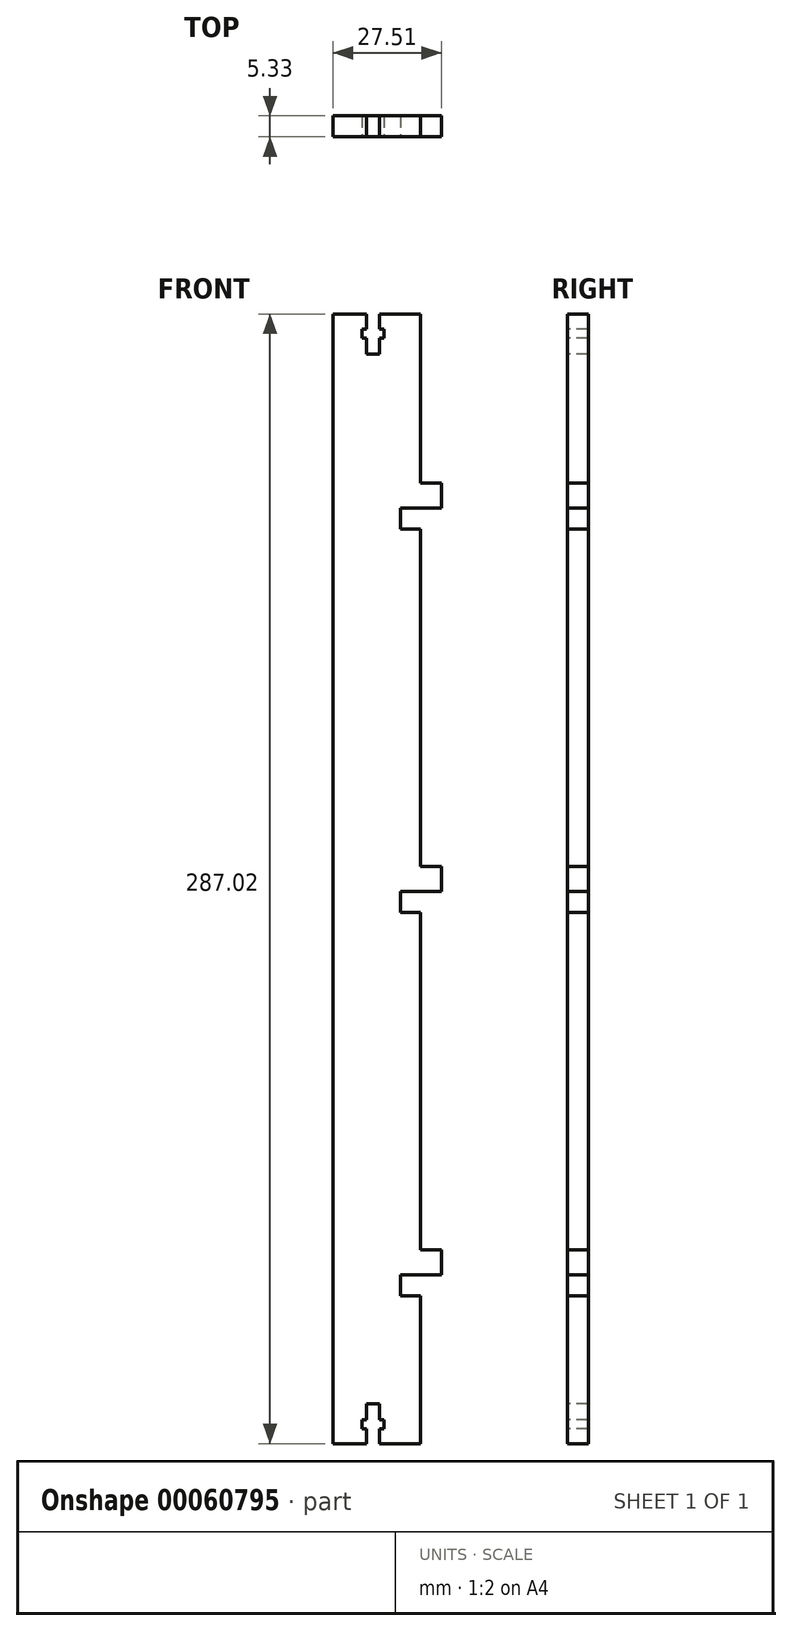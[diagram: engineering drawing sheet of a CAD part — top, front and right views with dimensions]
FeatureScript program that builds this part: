
annotation { "Feature Type Name" : "Feature", "Feature Type Description" : "" }
export const myFeature = defineFeature(function(context is Context, id is Id, definition is map)
    precondition{}
    {
        {
            var Q0;
            Q0=qCreatedBy(makeId("Front.planeOp"),FACE);
            var sketch = newSketch(context, id + "F0", { "sketchPlane" : qUnion([Q0])});
            skLineSegment(sketch, "E0.bottom", {"start": v(-34.55, 214.35) * mm, "end": v(-12.38, 214.35) * mm});
            skLineSegment(sketch, "E0.top", {"start": v(-34.55, -77.75) * mm, "end": v(-12.38, -77.75) * mm});
            skLineSegment(sketch, "E0.left", {"start": v(-34.55, 214.35) * mm, "end": v(-34.55, -77.75) * mm});
            skLineSegment(sketch, "E0.right", {"start": v(-12.38, 214.35) * mm, "end": v(-12.38, -77.75) * mm});
            skSolve(sketch);
        }
        {
            var Q0;
            Q0=makeQuery(id+"F0.imprint","IMPRINT",FACE,{"disambiguationData":[TD([[makeQuery(id+"F0.imprint","IMPRINT",EDGE,{"derivedFrom":sQuery(id+"F0.wireOp",EDGE,"E0.bottom")}),-1.0]])]});
            extrude(context, id + "F1", {"entities" : qUnion([Q0]), "depth" : 5.33 * mm});
        }
        {
            var Q0;
            Q0=makeQuery(id+"F1.opExtrude","SWEPT_FACE",FACE,{"disambiguationData":[OSD([sQuery(id+"F0.wireOp",EDGE,"E0.right")])]});
            var sketch = newSketch(context, id + "F2", { "sketchPlane" : qUnion([Q0])});
            skLineSegment(sketch, "E1.bottom", {"start": v(-5.33, 168.88) * mm, "end": v(0, 168.88) * mm});
            skLineSegment(sketch, "E1.top", {"start": v(-5.33, 162.53) * mm, "end": v(0, 162.53) * mm});
            skLineSegment(sketch, "E1.left", {"start": v(-5.33, 168.88) * mm, "end": v(-5.33, 162.53) * mm});
            skLineSegment(sketch, "E1.right", {"start": v(0, 168.88) * mm, "end": v(0, 162.53) * mm});
            skLineSegment(sketch, "E2.bottom", {"start": v(-5.33, 71.47) * mm, "end": v(0, 71.47) * mm});
            skLineSegment(sketch, "E2.top", {"start": v(-5.33, 65.12) * mm, "end": v(0, 65.12) * mm});
            skLineSegment(sketch, "E2.left", {"start": v(-5.33, 71.47) * mm, "end": v(-5.33, 65.12) * mm});
            skLineSegment(sketch, "E2.right", {"start": v(0, 71.47) * mm, "end": v(0, 65.12) * mm});
            skLineSegment(sketch, "E3.bottom", {"start": v(0, -25.94) * mm, "end": v(-5.33, -25.94) * mm});
            skLineSegment(sketch, "E3.top", {"start": v(0, -32.29) * mm, "end": v(-5.33, -32.29) * mm});
            skLineSegment(sketch, "E3.left", {"start": v(0, -25.94) * mm, "end": v(0, -32.29) * mm});
            skLineSegment(sketch, "E3.right", {"start": v(-5.33, -25.94) * mm, "end": v(-5.33, -32.29) * mm});
            skSolve(sketch);
        }
        {
            var Q0;
            Q0=makeQuery(id+"F2.imprint","IMPRINT",FACE,{"disambiguationData":[TD([[makeQuery(id+"F2.imprint","IMPRINT",EDGE,{"derivedFrom":sQuery(id+"F2.wireOp",EDGE,"E1.bottom")}),-1.0]])]});
            var Q1;
            Q1=makeQuery(id+"F2.imprint","IMPRINT",FACE,{"disambiguationData":[TD([[makeQuery(id+"F2.imprint","IMPRINT",EDGE,{"derivedFrom":sQuery(id+"F2.wireOp",EDGE,"E2.bottom")}),-1.0]])]});
            var Q2;
            Q2=makeQuery(id+"F2.imprint","IMPRINT",FACE,{"disambiguationData":[TD([[makeQuery(id+"F2.imprint","IMPRINT",EDGE,{"derivedFrom":sQuery(id+"F2.wireOp",EDGE,"E3.bottom")}),1.0]])]});
            extrude(context, id + "F3", {"entities" : qUnion([Q0, Q1, Q2]), "operationType" : NewBodyOperationType.ADD, "depth" : 5.33 * mm});
        }
        {
            var Q0;
            Q0=makeQuery(id+"F1.opExtrude","CAP_FACE",FACE,{"disambiguationData":[OSD([sQuery(id+"F0.wireOp",EDGE,"E0.bottom"),sQuery(id+"F0.wireOp",EDGE,"E0.top"),sQuery(id+"F0.wireOp",EDGE,"E0.left"),sQuery(id+"F0.wireOp",EDGE,"E0.right")])],"isStart":false});
            var sketch = newSketch(context, id + "F4", { "sketchPlane" : qUnion([Q0])});
            skLineSegment(sketch, "E4", {"start": v(-22.28, 68.3) * mm, "end": v(-43.85, 68.3) * mm});
            skLineSegment(sketch, "E5.left", {"start": v(-26.04, -77.75) * mm, "end": v(-26.04, -71.4) * mm});
            skLineSegment(sketch, "E5.right", {"start": v(-22.74, -77.75) * mm, "end": v(-22.74, -71.4) * mm});
            skLineSegment(sketch, "E6.0", {"start": v(-26.04, -71.4) * mm, "end": v(-27.19, -71.4) * mm});
            skLineSegment(sketch, "E7.bottom", {"start": v(-27.19, -71.4) * mm, "end": v(-26.04, -71.4) * mm});
            skLineSegment(sketch, "E7.top", {"start": v(-27.19, -69.12) * mm, "end": v(-26.04, -69.12) * mm});
            skLineSegment(sketch, "E7.left", {"start": v(-27.19, -71.4) * mm, "end": v(-27.19, -69.12) * mm});
            skLineSegment(sketch, "E7.right", {"start": v(-21.6, -71.4) * mm, "end": v(-21.6, -69.12) * mm});
            skLineSegment(sketch, "E8.trimOffspring", {"start": v(-26.04, -69.12) * mm, "end": v(-26.04, -65.05) * mm});
            skLineSegment(sketch, "E9.trimOffspring", {"start": v(-22.74, -69.12) * mm, "end": v(-22.74, -65.05) * mm});
            skLineSegment(sketch, "E10.trimOffspring", {"start": v(-22.74, -71.4) * mm, "end": v(-21.6, -71.4) * mm});
            skLineSegment(sketch, "E11.trimOffspring", {"start": v(-22.74, -69.12) * mm, "end": v(-21.6, -69.12) * mm});
            skLineSegment(sketch, "E12", {"start": v(-26.04, -77.75) * mm, "end": v(-22.74, -77.75) * mm});
            skLineSegment(sketch, "E13.0", {"start": v(-26.04, -65.05) * mm, "end": v(-22.74, -65.05) * mm});
            skLineSegment(sketch, "E14.MirrorCS", {"start": v(-26.04, 208) * mm, "end": v(-27.19, 208) * mm});
            skLineSegment(sketch, "E15.MirrorCS", {"start": v(-27.19, 208) * mm, "end": v(-26.04, 208) * mm});
            skLineSegment(sketch, "E16.MirrorCS", {"start": v(-21.6, 208) * mm, "end": v(-21.6, 205.7) * mm});
            skLineSegment(sketch, "E17.MirrorCS", {"start": v(-22.74, 208) * mm, "end": v(-21.6, 208) * mm});
            skLineSegment(sketch, "E18.MirrorCS", {"start": v(-22.74, 205.7) * mm, "end": v(-21.6, 205.7) * mm});
            skLineSegment(sketch, "E19.MirrorCS", {"start": v(-26.04, 214.35) * mm, "end": v(-22.74, 214.35) * mm});
            skLineSegment(sketch, "E20.MirrorCS", {"start": v(-27.19, 205.7) * mm, "end": v(-26.04, 205.7) * mm});
            skLineSegment(sketch, "E21.MirrorCS", {"start": v(-27.19, 208) * mm, "end": v(-27.19, 205.7) * mm});
            skLineSegment(sketch, "E22.MirrorCS", {"start": v(-26.04, 201.65) * mm, "end": v(-22.74, 201.65) * mm});
            skLineSegment(sketch, "E23.MirrorCS", {"start": v(-22.74, 214.35) * mm, "end": v(-22.74, 208) * mm});
            skLineSegment(sketch, "E24.MirrorCS", {"start": v(-22.74, 205.7) * mm, "end": v(-22.74, 201.65) * mm});
            skLineSegment(sketch, "E25.MirrorCS", {"start": v(-26.04, 214.35) * mm, "end": v(-26.04, 208) * mm});
            skLineSegment(sketch, "E26.MirrorCS", {"start": v(-26.04, 205.7) * mm, "end": v(-26.04, 201.65) * mm});
            skSolve(sketch);
        }
        {
            var Q0;
            Q0 = qSketchRegion(id + "F4", true);
            extrude(context, id + "F5", {"entities" : qUnion([Q0]), "operationType" : NewBodyOperationType.REMOVE, "endBound" : BoundingType.THROUGH_ALL, "oppositeDirection" : true, "depth" : 25.4 * mm});
        }
        {
            var Q0;
            Q0=makeQuery(id+"F3.boolean.opBoolean","MERGE",FACE,{"derivedFrom":[makeQuery(id+"F1.opExtrude","CAP_FACE",FACE,{"disambiguationData":[OSD([sQuery(id+"F0.wireOp",EDGE,"E0.bottom"),sQuery(id+"F0.wireOp",EDGE,"E0.top"),sQuery(id+"F0.wireOp",EDGE,"E0.left"),sQuery(id+"F0.wireOp",EDGE,"E0.right")])],"isStart":false}),makeQuery(id+"F3.opExtrude","SWEPT_FACE",FACE,{"disambiguationData":[OSD([sQuery(id+"F2.wireOp",EDGE,"E1.left")])]}),makeQuery(id+"F3.opExtrude","SWEPT_FACE",FACE,{"disambiguationData":[OSD([sQuery(id+"F2.wireOp",EDGE,"E2.left")])]}),makeQuery(id+"F3.opExtrude","SWEPT_FACE",FACE,{"disambiguationData":[OSD([sQuery(id+"F2.wireOp",EDGE,"E3.right")])]})]});
            var sketch = newSketch(context, id + "F6", { "sketchPlane" : qUnion([Q0])});
            skLineSegment(sketch, "E27.bottom", {"start": v(-12.38, 162.53) * mm, "end": v(-17.46, 162.53) * mm});
            skLineSegment(sketch, "E27.top", {"start": v(-12.38, 157.2) * mm, "end": v(-17.46, 157.2) * mm});
            skLineSegment(sketch, "E27.left", {"start": v(-12.38, 162.53) * mm, "end": v(-12.38, 157.2) * mm});
            skLineSegment(sketch, "E27.right", {"start": v(-17.46, 162.53) * mm, "end": v(-17.46, 157.2) * mm});
            skLineSegment(sketch, "E28.bottom", {"start": v(-12.38, 65.12) * mm, "end": v(-17.46, 65.12) * mm});
            skLineSegment(sketch, "E28.top", {"start": v(-12.38, 59.79) * mm, "end": v(-17.46, 59.79) * mm});
            skLineSegment(sketch, "E28.left", {"start": v(-12.38, 65.12) * mm, "end": v(-12.38, 59.79) * mm});
            skLineSegment(sketch, "E28.right", {"start": v(-17.46, 65.12) * mm, "end": v(-17.46, 59.79) * mm});
            skLineSegment(sketch, "E29.bottom", {"start": v(-12.38, -32.29) * mm, "end": v(-17.46, -32.29) * mm});
            skLineSegment(sketch, "E29.top", {"start": v(-12.38, -37.62) * mm, "end": v(-17.46, -37.62) * mm});
            skLineSegment(sketch, "E29.left", {"start": v(-12.38, -32.29) * mm, "end": v(-12.38, -37.62) * mm});
            skLineSegment(sketch, "E29.right", {"start": v(-17.46, -32.29) * mm, "end": v(-17.46, -37.62) * mm});
            skSolve(sketch);
        }
        {
            var Q0;
            Q0 = qSketchRegion(id + "F6", true);
            extrude(context, id + "F7", {"entities" : qUnion([Q0]), "operationType" : NewBodyOperationType.REMOVE, "oppositeDirection" : true, "depth" : 25.4 * mm});
        }
        {
            var Q0;
            Q0=makeQuery(id+"F3.boolean.opBoolean","MERGE",FACE,{"derivedFrom":[makeQuery(id+"F1.opExtrude","CAP_FACE",FACE,{"disambiguationData":[OSD([sQuery(id+"F0.wireOp",EDGE,"E0.bottom"),sQuery(id+"F0.wireOp",EDGE,"E0.top"),sQuery(id+"F0.wireOp",EDGE,"E0.left"),sQuery(id+"F0.wireOp",EDGE,"E0.right")])],"isStart":false}),makeQuery(id+"F3.opExtrude","SWEPT_FACE",FACE,{"disambiguationData":[OSD([sQuery(id+"F2.wireOp",EDGE,"E1.left")])]}),makeQuery(id+"F3.opExtrude","SWEPT_FACE",FACE,{"disambiguationData":[OSD([sQuery(id+"F2.wireOp",EDGE,"E2.left")])]}),makeQuery(id+"F3.opExtrude","SWEPT_FACE",FACE,{"disambiguationData":[OSD([sQuery(id+"F2.wireOp",EDGE,"E3.right")])]})]});
            var sketch = newSketch(context, id + "F8", { "sketchPlane" : qUnion([Q0])});
            skLineSegment(sketch, "E30.bottom", {"start": v(-12.38, 214.35) * mm, "end": v(-34.55, 214.35) * mm});
            skLineSegment(sketch, "E30.top", {"start": v(-12.38, 211.8) * mm, "end": v(-34.55, 211.8) * mm});
            skLineSegment(sketch, "E30.left", {"start": v(-12.38, 214.35) * mm, "end": v(-12.38, 211.8) * mm});
            skLineSegment(sketch, "E30.right", {"start": v(-34.55, 214.35) * mm, "end": v(-34.55, 211.8) * mm});
            skLineSegment(sketch, "E31.bottom", {"start": v(-12.38, -77.75) * mm, "end": v(-34.55, -77.75) * mm});
            skLineSegment(sketch, "E31.top", {"start": v(-12.38, -75.21) * mm, "end": v(-34.55, -75.21) * mm});
            skLineSegment(sketch, "E31.left", {"start": v(-12.38, -77.75) * mm, "end": v(-12.38, -75.21) * mm});
            skLineSegment(sketch, "E31.right", {"start": v(-34.55, -77.75) * mm, "end": v(-34.55, -75.21) * mm});
            skSolve(sketch);
        }
        {
            var Q0;
            Q0 = qSketchRegion(id + "F8", true);
            extrude(context, id + "F9", {"entities" : qUnion([Q0]), "operationType" : NewBodyOperationType.REMOVE, "oppositeDirection" : true, "depth" : 25.4 * mm});
        }
    });
